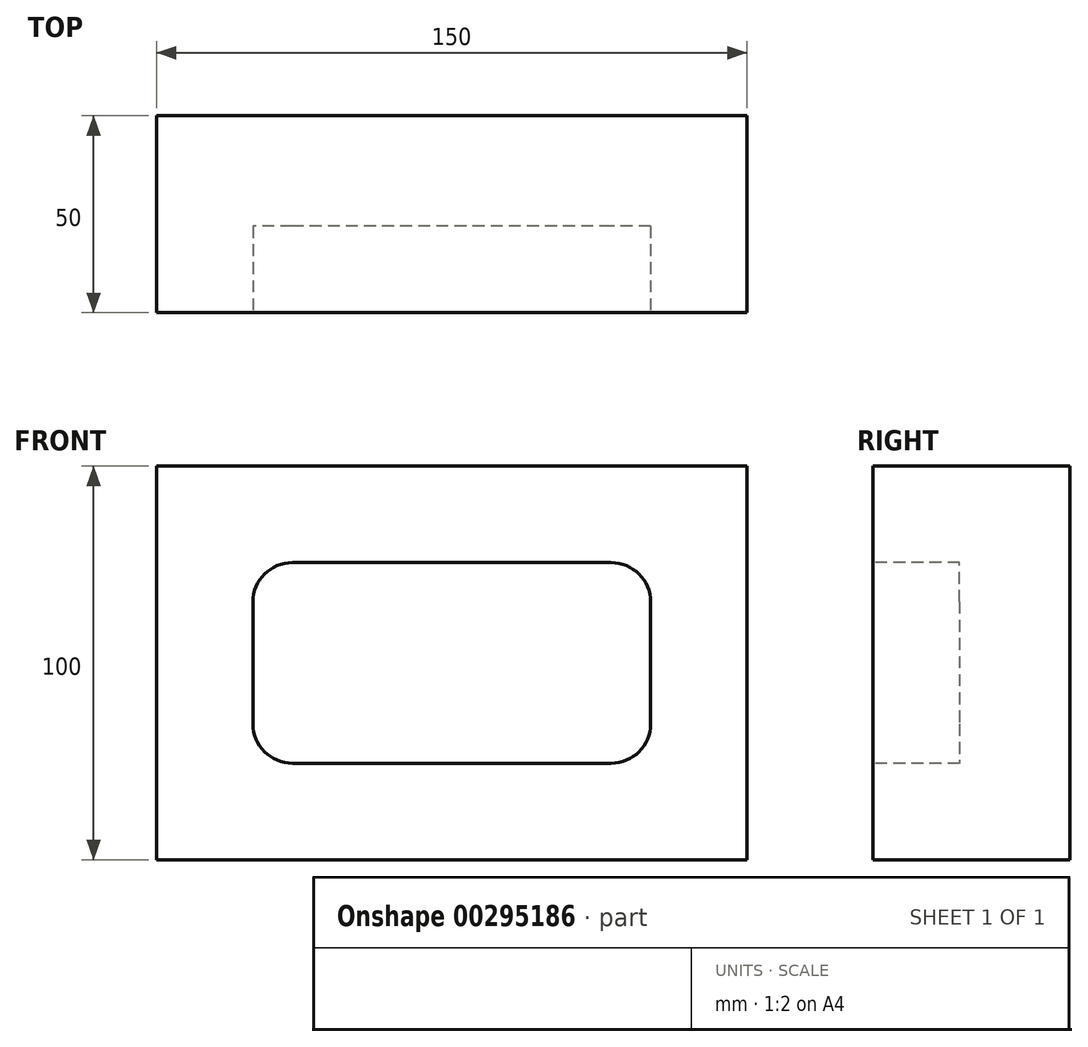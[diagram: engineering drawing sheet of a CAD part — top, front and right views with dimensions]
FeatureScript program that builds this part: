
annotation { "Feature Type Name" : "Feature", "Feature Type Description" : "" }
export const myFeature = defineFeature(function(context is Context, id is Id, definition is map)
    precondition{}
    {
        {
            var Q0;
            Q0=qCreatedBy(makeId("Front.planeOp"),FACE);
            var sketch = newSketch(context, id + "F0", { "sketchPlane" : qUnion([Q0])});
            skLineSegment(sketch, "E0.bottom", {"start": v(-75, 50) * mm, "end": v(75, 50) * mm});
            skLineSegment(sketch, "E0.top", {"start": v(-75, -50) * mm, "end": v(75, -50) * mm});
            skLineSegment(sketch, "E0.left", {"start": v(-75, 50) * mm, "end": v(-75, -50) * mm});
            skLineSegment(sketch, "E0.right", {"start": v(75, 50) * mm, "end": v(75, -50) * mm});
            skPoint(sketch, "E0.middle", {"position": v(0, 0) * mm});
            skSolve(sketch);
        }
        {
            var Q0;
            Q0=makeQuery(id+"F0.imprint","IMPRINT",FACE,{"disambiguationData":[TD([[makeQuery(id+"F0.imprint","IMPRINT",EDGE,{"derivedFrom":sQuery(id+"F0.wireOp",EDGE,"E0.bottom")}),-1.0]])]});
            extrude(context, id + "F1", {"entities" : qUnion([Q0]), "depth" : 50 * mm});
        }
        {
            var Q0;
            Q0=makeQuery(id+"F1.opExtrude","CAP_FACE",FACE,{"disambiguationData":[OSD([sQuery(id+"F0.wireOp",EDGE,"E0.bottom"),sQuery(id+"F0.wireOp",EDGE,"E0.top"),sQuery(id+"F0.wireOp",EDGE,"E0.left"),sQuery(id+"F0.wireOp",EDGE,"E0.right")])],"isStart":false});
            var sketch = newSketch(context, id + "F2", { "sketchPlane" : qUnion([Q0])});
            skLineSegment(sketch, "E1.bottom", {"start": v(40.5, 25.5) * mm, "end": v(-40.5, 25.5) * mm});
            skLineSegment(sketch, "E1.top", {"start": v(40.5, -25.5) * mm, "end": v(-40.5, -25.5) * mm});
            skLineSegment(sketch, "E1.left", {"start": v(50.5, 15.5) * mm, "end": v(50.5, -15.5) * mm});
            skLineSegment(sketch, "E1.right", {"start": v(-50.5, 15.5) * mm, "end": v(-50.5, -15.5) * mm});
            skPoint(sketch, "E1.middle", {"position": v(0, 0) * mm});
            skPoint(sketch, "E2.visualSharp", {"position": v(-50.5, 25.5) * mm});
            skArc(sketch, "E2.filletArc", {"start": v(-40.5, 25.5) * mm, "mid": v(-47.57, 22.57) * mm, "end": v(-50.5, 15.5) * mm});
            skPoint(sketch, "E3.visualSharp", {"position": v(50.5, 25.5) * mm});
            skArc(sketch, "E3.filletArc", {"start": v(50.5, 15.5) * mm, "mid": v(47.57, 22.57) * mm, "end": v(40.5, 25.5) * mm});
            skPoint(sketch, "E4.visualSharp", {"position": v(50.5, -25.5) * mm});
            skArc(sketch, "E4.filletArc", {"start": v(40.5, -25.5) * mm, "mid": v(47.57, -22.57) * mm, "end": v(50.5, -15.5) * mm});
            skPoint(sketch, "E5.visualSharp", {"position": v(-50.5, -25.5) * mm});
            skArc(sketch, "E5.filletArc", {"start": v(-50.5, -15.5) * mm, "mid": v(-47.57, -22.57) * mm, "end": v(-40.5, -25.5) * mm});
            skSolve(sketch);
        }
        {
            var Q0;
            Q0=makeQuery(id+"F2.imprint","IMPRINT",FACE,{"disambiguationData":[TD([[makeQuery(id+"F2.imprint","IMPRINT",EDGE,{"derivedFrom":sQuery(id+"F2.wireOp",EDGE,"E1.bottom")}),1.0]])]});
            extrude(context, id + "F3", {"entities" : qUnion([Q0]), "operationType" : NewBodyOperationType.REMOVE, "oppositeDirection" : true, "depth" : 22 * mm});
        }
    });
